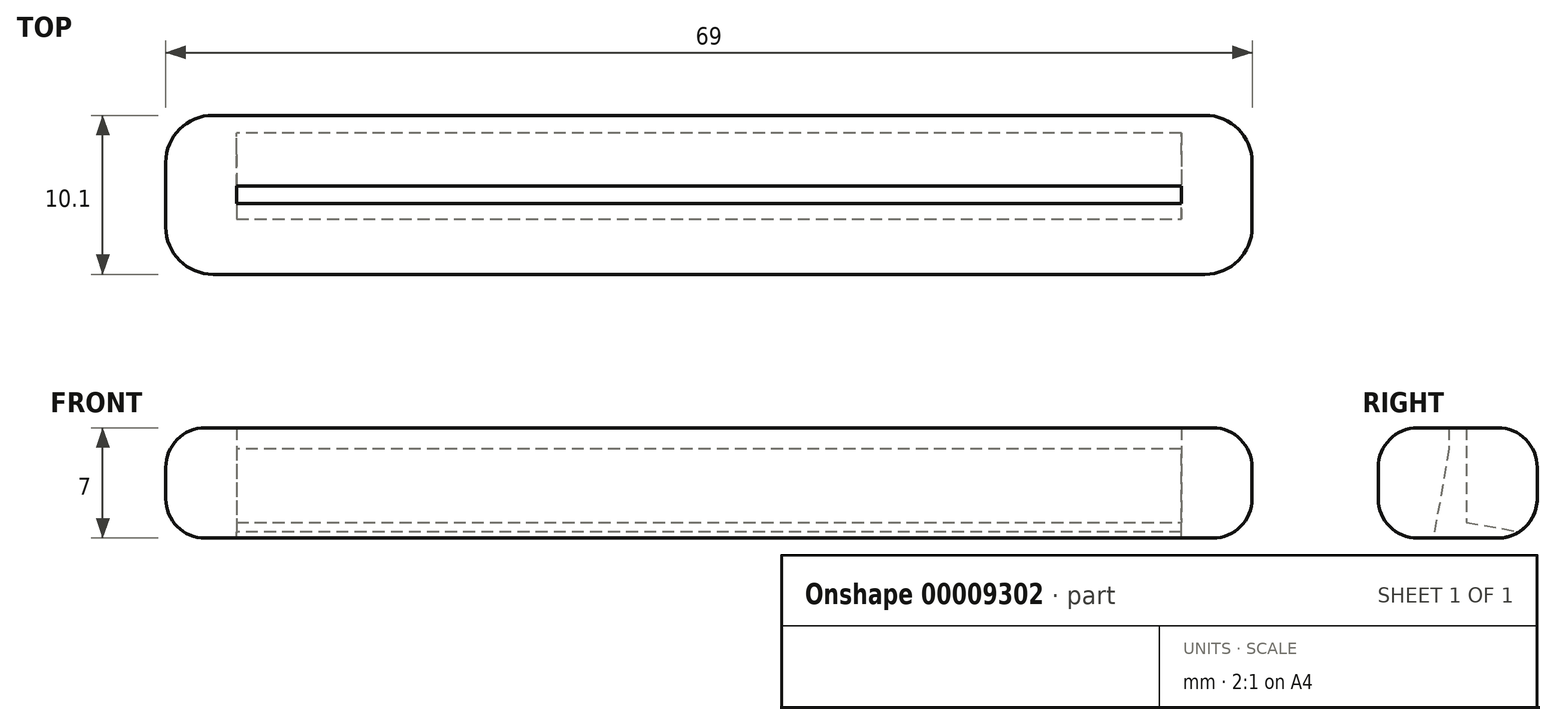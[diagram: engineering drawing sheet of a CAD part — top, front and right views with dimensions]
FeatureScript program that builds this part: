
annotation { "Feature Type Name" : "Feature", "Feature Type Description" : "" }
export const myFeature = defineFeature(function(context is Context, id is Id, definition is map)
    precondition{}
    {
        {
            var Q0;
            Q0=qCreatedBy(makeId("Top.planeOp"),FACE);
            var sketch = newSketch(context, id + "F0", { "sketchPlane" : qUnion([Q0])});
            skLineSegment(sketch, "E0.bottom", {"start": v(-31.18, 12.18) * mm, "end": v(28.82, 12.18) * mm});
            skLineSegment(sketch, "E0.top", {"start": v(-31.18, 11.08) * mm, "end": v(28.82, 11.08) * mm});
            skLineSegment(sketch, "E0.left", {"start": v(-31.18, 12.18) * mm, "end": v(-31.18, 11.08) * mm});
            skLineSegment(sketch, "E0.right", {"start": v(28.82, 12.18) * mm, "end": v(28.82, 11.08) * mm});
            skLineSegment(sketch, "E1.top", {"start": v(-32.68, 6.58) * mm, "end": v(30.32, 6.58) * mm});
            skLineSegment(sketch, "E1.left", {"start": v(-35.68, 13.68) * mm, "end": v(-35.68, 9.58) * mm});
            skPoint(sketch, "E2.visualSharp", {"position": v(-35.68, 6.58) * mm});
            skArc(sketch, "E2.filletArc", {"start": v(-35.68, 9.58) * mm, "mid": v(-34.8, 7.46) * mm, "end": v(-32.68, 6.58) * mm});
            skLineSegment(sketch, "E3", {"start": v(-1.18, 12.18) * mm, "end": v(-1.18, 24.22) * mm, "construction": true});
            skLineSegment(sketch, "E4", {"start": v(-1.18, 12.18) * mm, "end": v(-1.18, -0.18) * mm, "construction": true});
            skPoint(sketch, "E4.endSnap0", {"position": v(-1.18, 11.08) * mm});
            skLineSegment(sketch, "E5.MirrorCS", {"start": v(33.32, 13.68) * mm, "end": v(33.32, 9.58) * mm});
            skArc(sketch, "E6.MirrorCS", {"start": v(33.32, 9.58) * mm, "mid": v(32.44, 7.46) * mm, "end": v(30.32, 6.58) * mm});
            skLineSegment(sketch, "E7", {"start": v(-31.18, 11.63) * mm, "end": v(-37.06, 11.63) * mm, "construction": true});
            skArc(sketch, "E8.MirrorCS", {"start": v(-35.68, 13.68) * mm, "mid": v(-34.8, 15.8) * mm, "end": v(-32.68, 16.68) * mm});
            skLineSegment(sketch, "E9.MirrorCS", {"start": v(-32.68, 16.68) * mm, "end": v(30.32, 16.68) * mm});
            skArc(sketch, "E10.MirrorCS", {"start": v(33.32, 13.68) * mm, "mid": v(32.44, 15.8) * mm, "end": v(30.32, 16.68) * mm});
            skSolve(sketch);
        }
        {
            var Q0;
            Q0=makeQuery(id+"F0.imprint","IMPRINT",FACE,{"disambiguationData":[TD([[makeQuery(id+"F0.imprint","IMPRINT",EDGE,{"derivedFrom":sQuery(id+"F0.wireOp",EDGE,"E0.bottom")}),1.0]])]});
            extrude(context, id + "F1", {"entities" : qUnion([Q0]), "depth" : 7 * mm});
        }
        {
            var Q0;
            Q0=makeQuery(id+"F1.opExtrude","CAP_EDGE",EDGE,{"disambiguationData":[OSD([sQuery(id+"F0.wireOp",EDGE,"E1.top")])],"isStart":false});
            fillet(context, id + "F2", {"entities" : qUnion([Q0]), "radius" : 2.5 * mm, "tangentPropagation" : true, "allowEdgeOverflow" : false});
        }
        {
            var Q0;
            Q0=makeQuery(id+"F1.opExtrude","CAP_EDGE",EDGE,{"disambiguationData":[OSD([sQuery(id+"F0.wireOp",EDGE,"E1.top")])],"isStart":true});
            fillet(context, id + "F3", {"entities" : qUnion([Q0]), "radius" : 2.5 * mm, "tangentPropagation" : true, "allowEdgeOverflow" : false});
        }
        {
            var Q0;
            Q0=makeQuery(id+"F1.opExtrude","CAP_EDGE",EDGE,{"disambiguationData":[OSD([sQuery(id+"F0.wireOp",EDGE,"E0.top")])],"isStart":true});
            var Q1;
            Q1=makeQuery(id+"F1.opExtrude","CAP_EDGE",EDGE,{"disambiguationData":[OSD([sQuery(id+"F0.wireOp",EDGE,"E0.bottom")])],"isStart":true});
            chamfer(context, id + "F4", {"entities" : qUnion([Q0, Q1]), "chamferType" : ChamferType.OFFSET_ANGLE, "width" : 1 * mm, "oppositeDirection" : false, "angle" : 80 * degree, "tangentPropagation" : true});
        }
    });
